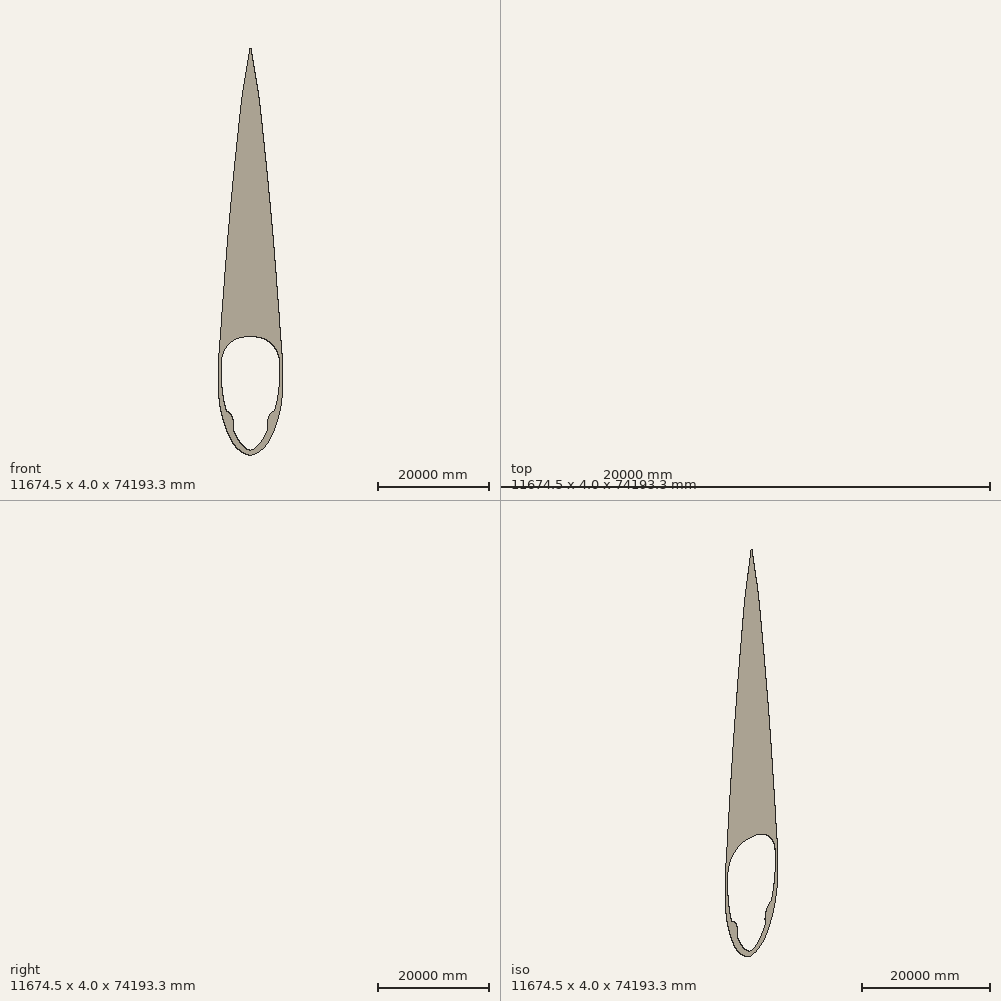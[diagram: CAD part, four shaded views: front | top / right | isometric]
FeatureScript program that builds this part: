
annotation { "Feature Type Name" : "Feature", "Feature Type Description" : "" }
export const myFeature = defineFeature(function(context is Context, id is Id, definition is map)
    precondition{}
    {
        {
            var Q0;
            Q0=qCreatedBy(makeId("Front.planeOp"),FACE);
            var sketch = newSketch(context, id + "F0", { "sketchPlane" : qUnion([Q0])});
            skLineSegment(sketch, "E0", {"start": v(0, -37096.65) * mm, "end": v(-23.06, -36971.76) * mm});
            skLineSegment(sketch, "E1", {"start": v(-23.06, -36971.76) * mm, "end": v(0, -37096.65) * mm});
            skLineSegment(sketch, "E2", {"start": v(0, -37096.65) * mm, "end": v(-199.5, -37059.82) * mm});
            skLineSegment(sketch, "E3", {"start": v(-199.5, -37059.82) * mm, "end": v(-412.04, -37002.75) * mm});
            skLineSegment(sketch, "E4", {"start": v(-412.04, -37002.75) * mm, "end": v(-621.33, -36933.84) * mm});
            skLineSegment(sketch, "E5", {"start": v(-621.33, -36933.84) * mm, "end": v(-815.34, -36864.47) * mm});
            skLineSegment(sketch, "E6", {"start": v(-815.34, -36864.47) * mm, "end": v(-1006.9, -36788.7) * mm});
            skLineSegment(sketch, "E7", {"start": v(-1006.9, -36788.7) * mm, "end": v(-1256.13, -36672.62) * mm});
            skLineSegment(sketch, "E8", {"start": v(-1256.13, -36672.62) * mm, "end": v(-1493.88, -36535.36) * mm});
            skLineSegment(sketch, "E9", {"start": v(-1493.88, -36535.36) * mm, "end": v(-1681.02, -36403.79) * mm});
            skLineSegment(sketch, "E10", {"start": v(-1681.02, -36403.79) * mm, "end": v(-1862.46, -36263.7) * mm});
            skLineSegment(sketch, "E11", {"start": v(-1862.46, -36263.7) * mm, "end": v(-2090.12, -36083.09) * mm});
            skLineSegment(sketch, "E12", {"start": v(-2090.12, -36083.09) * mm, "end": v(-2309.52, -35893.5) * mm});
            skLineSegment(sketch, "E13", {"start": v(-2309.52, -35893.5) * mm, "end": v(-2502.76, -35700.77) * mm});
            skLineSegment(sketch, "E14", {"start": v(-2502.76, -35700.77) * mm, "end": v(-2686.25, -35497.97) * mm});
            skLineSegment(sketch, "E15", {"start": v(-2686.25, -35497.97) * mm, "end": v(-2852.5, -35302.42) * mm});
            skLineSegment(sketch, "E16", {"start": v(-2852.5, -35302.42) * mm, "end": v(-3008.15, -35098.91) * mm});
            skLineSegment(sketch, "E17", {"start": v(-3008.15, -35098.91) * mm, "end": v(-3148.76, -34887.5) * mm});
            skLineSegment(sketch, "E18", {"start": v(-3148.76, -34887.5) * mm, "end": v(-3283.5, -34672.02) * mm});
            skLineSegment(sketch, "E19", {"start": v(-3283.5, -34672.02) * mm, "end": v(-3175.84, -34604.68) * mm});
            skLineSegment(sketch, "E20", {"start": v(-3175.84, -34604.68) * mm, "end": v(-3283.5, -34672.02) * mm});
            skLineSegment(sketch, "E21", {"start": v(-3283.5, -34672.02) * mm, "end": v(-3291.13, -34659.95) * mm});
            skLineSegment(sketch, "E22", {"start": v(-3291.13, -34659.95) * mm, "end": v(-3183.46, -34592.62) * mm});
            skLineSegment(sketch, "E23", {"start": v(-3183.46, -34592.62) * mm, "end": v(-3291.13, -34659.95) * mm});
            skLineSegment(sketch, "E24", {"start": v(-3291.13, -34659.95) * mm, "end": v(-3416.73, -34462.67) * mm});
            skLineSegment(sketch, "E25", {"start": v(-3416.73, -34462.67) * mm, "end": v(-3537.36, -34262.54) * mm});
            skLineSegment(sketch, "E26", {"start": v(-3537.36, -34262.54) * mm, "end": v(-3671.16, -34003.59) * mm});
            skLineSegment(sketch, "E27", {"start": v(-3671.16, -34003.59) * mm, "end": v(-3795.65, -33739.48) * mm});
            skLineSegment(sketch, "E28", {"start": v(-3795.65, -33739.48) * mm, "end": v(-3922.1, -33474.79) * mm});
            skLineSegment(sketch, "E29", {"start": v(-3922.1, -33474.79) * mm, "end": v(-4045.76, -33209.05) * mm});
            skLineSegment(sketch, "E30", {"start": v(-4045.76, -33209.05) * mm, "end": v(-4144.21, -32979.77) * mm});
            skLineSegment(sketch, "E31", {"start": v(-4144.21, -32979.77) * mm, "end": v(-4236.97, -32748.02) * mm});
            skLineSegment(sketch, "E32", {"start": v(-4236.97, -32748.02) * mm, "end": v(-4415.51, -32278.83) * mm});
            skLineSegment(sketch, "E33", {"start": v(-4415.51, -32278.83) * mm, "end": v(-4513.17, -32023.6) * mm});
            skLineSegment(sketch, "E34", {"start": v(-4513.17, -32023.6) * mm, "end": v(-4608.2, -31767.42) * mm});
            skLineSegment(sketch, "E35", {"start": v(-4608.2, -31767.42) * mm, "end": v(-4705.45, -31481.47) * mm});
            skLineSegment(sketch, "E36", {"start": v(-4705.45, -31481.47) * mm, "end": v(-4795.6, -31193.16) * mm});
            skLineSegment(sketch, "E37", {"start": v(-4795.6, -31193.16) * mm, "end": v(-4908.47, -30801.92) * mm});
            skLineSegment(sketch, "E38", {"start": v(-4908.47, -30801.92) * mm, "end": v(-4786.45, -30766.72) * mm});
            skLineSegment(sketch, "E39", {"start": v(-4786.45, -30766.72) * mm, "end": v(-4908.47, -30801.92) * mm});
            skLineSegment(sketch, "E40", {"start": v(-4908.47, -30801.92) * mm, "end": v(-4964.13, -30600.88) * mm});
            skLineSegment(sketch, "E41", {"start": v(-4964.13, -30600.88) * mm, "end": v(-5135.78, -29969.28) * mm});
            skLineSegment(sketch, "E42", {"start": v(-5135.78, -29969.28) * mm, "end": v(-5236.18, -29587.47) * mm});
            skLineSegment(sketch, "E43", {"start": v(-5236.18, -29587.47) * mm, "end": v(-5325.57, -29203.14) * mm});
            skLineSegment(sketch, "E44", {"start": v(-5325.57, -29203.14) * mm, "end": v(-5382.36, -28908.63) * mm});
            skLineSegment(sketch, "E45", {"start": v(-5382.36, -28908.63) * mm, "end": v(-5437.78, -28613.76) * mm});
            skLineSegment(sketch, "E46", {"start": v(-5437.78, -28613.76) * mm, "end": v(-5477.92, -28417.57) * mm});
            skLineSegment(sketch, "E47", {"start": v(-5477.92, -28417.57) * mm, "end": v(-5516.47, -28221.15) * mm});
            skLineSegment(sketch, "E48", {"start": v(-5516.47, -28221.15) * mm, "end": v(-5570.14, -27874.09) * mm});
            skLineSegment(sketch, "E49", {"start": v(-5570.14, -27874.09) * mm, "end": v(-5613.73, -27525.35) * mm});
            skLineSegment(sketch, "E50", {"start": v(-5613.73, -27525.35) * mm, "end": v(-5665.85, -27100.86) * mm});
            skLineSegment(sketch, "E51", {"start": v(-5665.85, -27100.86) * mm, "end": v(-5713.76, -26676.05) * mm});
            skLineSegment(sketch, "E52", {"start": v(-5713.76, -26676.05) * mm, "end": v(-5587.57, -26661.8) * mm});
            skLineSegment(sketch, "E53", {"start": v(-5587.57, -26661.8) * mm, "end": v(-5713.76, -26676.05) * mm});
            skLineSegment(sketch, "E54", {"start": v(-5713.76, -26676.05) * mm, "end": v(-5718, -26633.9) * mm});
            skLineSegment(sketch, "E55", {"start": v(-5718, -26633.9) * mm, "end": v(-5752.41, -26236.68) * mm});
            skLineSegment(sketch, "E56", {"start": v(-5752.41, -26236.68) * mm, "end": v(-5778.7, -25838.78) * mm});
            skLineSegment(sketch, "E57", {"start": v(-5778.7, -25838.78) * mm, "end": v(-5800.12, -25414.8) * mm});
            skLineSegment(sketch, "E58", {"start": v(-5800.12, -25414.8) * mm, "end": v(-5815.13, -24990.58) * mm});
            skLineSegment(sketch, "E59", {"start": v(-5815.13, -24990.58) * mm, "end": v(-5830.06, -24103.63) * mm});
            skLineSegment(sketch, "E60", {"start": v(-5830.06, -24103.63) * mm, "end": v(-5837.25, -22774.4) * mm});
            skLineSegment(sketch, "E61", {"start": v(-5837.25, -22774.4) * mm, "end": v(-5835.85, -22468.92) * mm});
            skLineSegment(sketch, "E62", {"start": v(-5835.85, -22468.92) * mm, "end": v(-5708.85, -22469.5) * mm});
            skLineSegment(sketch, "E63", {"start": v(-5708.85, -22469.5) * mm, "end": v(-5835.85, -22468.92) * mm});
            skLineSegment(sketch, "E64", {"start": v(-5835.85, -22468.92) * mm, "end": v(-5824.1, -21345.02) * mm});
            skLineSegment(sketch, "E65", {"start": v(-5824.1, -21345.02) * mm, "end": v(-5817.29, -20813.75) * mm});
            skLineSegment(sketch, "E66", {"start": v(-5817.29, -20813.75) * mm, "end": v(-5805.37, -20282.59) * mm});
            skLineSegment(sketch, "E67", {"start": v(-5805.37, -20282.59) * mm, "end": v(-5782.67, -19739.46) * mm});
            skLineSegment(sketch, "E68", {"start": v(-5782.67, -19739.46) * mm, "end": v(-5747.26, -19197.02) * mm});
            skLineSegment(sketch, "E69", {"start": v(-5747.26, -19197.02) * mm, "end": v(-5713.76, -18798.26) * mm});
            skLineSegment(sketch, "E70", {"start": v(-5713.76, -18798.26) * mm, "end": v(-5680.74, -18399.48) * mm});
            skLineSegment(sketch, "E71", {"start": v(-5680.74, -18399.48) * mm, "end": v(-5670.8, -18263.2) * mm});
            skLineSegment(sketch, "E72", {"start": v(-5670.8, -18263.2) * mm, "end": v(-5544.13, -18272.43) * mm});
            skLineSegment(sketch, "E73", {"start": v(-5544.13, -18272.43) * mm, "end": v(-5670.8, -18263.2) * mm});
            skLineSegment(sketch, "E74", {"start": v(-5670.8, -18263.2) * mm, "end": v(-5626.79, -17613.9) * mm});
            skLineSegment(sketch, "E75", {"start": v(-5626.79, -17613.9) * mm, "end": v(-5564.33, -16875.94) * mm});
            skLineSegment(sketch, "E76", {"start": v(-5564.33, -16875.94) * mm, "end": v(-5451.63, -15470.8) * mm});
            skLineSegment(sketch, "E77", {"start": v(-5451.63, -15470.8) * mm, "end": v(-5351.12, -14064.74) * mm});
            skLineSegment(sketch, "E78", {"start": v(-5351.12, -14064.74) * mm, "end": v(-5224.45, -14073.78) * mm});
            skLineSegment(sketch, "E79", {"start": v(-5224.45, -14073.78) * mm, "end": v(-5351.12, -14064.74) * mm});
            skLineSegment(sketch, "E80", {"start": v(-5351.12, -14064.74) * mm, "end": v(-5174.97, -11416.08) * mm});
            skLineSegment(sketch, "E81", {"start": v(-5174.97, -11416.08) * mm, "end": v(-5048.25, -11424.51) * mm});
            skLineSegment(sketch, "E82", {"start": v(-5048.25, -11424.51) * mm, "end": v(-5174.97, -11416.08) * mm});
            skLineSegment(sketch, "E83", {"start": v(-5174.97, -11416.08) * mm, "end": v(-4896.69, -7799.65) * mm});
            skLineSegment(sketch, "E84", {"start": v(-4896.69, -7799.65) * mm, "end": v(-4770.04, -7809.4) * mm});
            skLineSegment(sketch, "E85", {"start": v(-4770.04, -7809.4) * mm, "end": v(-4896.69, -7799.65) * mm});
            skLineSegment(sketch, "E86", {"start": v(-4896.69, -7799.65) * mm, "end": v(-4548.63, -3176.4) * mm});
            skLineSegment(sketch, "E87", {"start": v(-4548.63, -3176.4) * mm, "end": v(-4421.99, -3185.92) * mm});
            skLineSegment(sketch, "E88", {"start": v(-4421.99, -3185.92) * mm, "end": v(-4548.63, -3176.4) * mm});
            skLineSegment(sketch, "E89", {"start": v(-4548.63, -3176.4) * mm, "end": v(-4097.3, 2407.44) * mm});
            skLineSegment(sketch, "E90", {"start": v(-4097.3, 2407.44) * mm, "end": v(-3970.73, 2397.2) * mm});
            skLineSegment(sketch, "E91", {"start": v(-3970.73, 2397.2) * mm, "end": v(-4097.3, 2407.44) * mm});
            skLineSegment(sketch, "E92", {"start": v(-4097.3, 2407.44) * mm, "end": v(-3754.7, 6281.67) * mm});
            skLineSegment(sketch, "E93", {"start": v(-3754.7, 6281.67) * mm, "end": v(-3628.21, 6270.5) * mm});
            skLineSegment(sketch, "E94", {"start": v(-3628.21, 6270.5) * mm, "end": v(-3754.7, 6281.67) * mm});
            skLineSegment(sketch, "E95", {"start": v(-3754.7, 6281.67) * mm, "end": v(-3346.15, 10484.71) * mm});
            skLineSegment(sketch, "E96", {"start": v(-3346.15, 10484.71) * mm, "end": v(-3219.75, 10472.42) * mm});
            skLineSegment(sketch, "E97", {"start": v(-3219.75, 10472.42) * mm, "end": v(-3346.15, 10484.71) * mm});
            skLineSegment(sketch, "E98", {"start": v(-3346.15, 10484.71) * mm, "end": v(-3071.3, 13448.2) * mm});
            skLineSegment(sketch, "E99", {"start": v(-3071.3, 13448.2) * mm, "end": v(-2944.83, 13436.47) * mm});
            skLineSegment(sketch, "E100", {"start": v(-2944.83, 13436.47) * mm, "end": v(-3071.3, 13448.2) * mm});
            skLineSegment(sketch, "E101", {"start": v(-3071.3, 13448.2) * mm, "end": v(-3028.06, 13918.2) * mm});
            skLineSegment(sketch, "E102", {"start": v(-3028.06, 13918.2) * mm, "end": v(-2984.83, 14278.46) * mm});
            skLineSegment(sketch, "E103", {"start": v(-2984.83, 14278.46) * mm, "end": v(-2942.77, 14638.8) * mm});
            skLineSegment(sketch, "E104", {"start": v(-2942.77, 14638.8) * mm, "end": v(-2910.05, 15016.99) * mm});
            skLineSegment(sketch, "E105", {"start": v(-2910.05, 15016.99) * mm, "end": v(-2879.8, 15395.47) * mm});
            skLineSegment(sketch, "E106", {"start": v(-2879.8, 15395.47) * mm, "end": v(-2810.46, 16049.37) * mm});
            skLineSegment(sketch, "E107", {"start": v(-2810.46, 16049.37) * mm, "end": v(-2718.18, 16865.3) * mm});
            skLineSegment(sketch, "E108", {"start": v(-2718.18, 16865.3) * mm, "end": v(-2641.02, 17547.39) * mm});
            skLineSegment(sketch, "E109", {"start": v(-2641.02, 17547.39) * mm, "end": v(-2602.15, 17952.92) * mm});
            skLineSegment(sketch, "E110", {"start": v(-2602.15, 17952.92) * mm, "end": v(-2564.33, 18358.56) * mm});
            skLineSegment(sketch, "E111", {"start": v(-2564.33, 18358.56) * mm, "end": v(-2476.75, 19167.53) * mm});
            skLineSegment(sketch, "E112", {"start": v(-2476.75, 19167.53) * mm, "end": v(-2368.14, 20139.23) * mm});
            skLineSegment(sketch, "E113", {"start": v(-2368.14, 20139.23) * mm, "end": v(-2264.77, 21133.64) * mm});
            skLineSegment(sketch, "E114", {"start": v(-2264.77, 21133.64) * mm, "end": v(-2207.67, 21721.47) * mm});
            skLineSegment(sketch, "E115", {"start": v(-2207.67, 21721.47) * mm, "end": v(-2148.26, 22309.05) * mm});
            skLineSegment(sketch, "E116", {"start": v(-2148.26, 22309.05) * mm, "end": v(-2083.49, 22880.75) * mm});
            skLineSegment(sketch, "E117", {"start": v(-2083.49, 22880.75) * mm, "end": v(-2012.62, 23451.72) * mm});
            skLineSegment(sketch, "E118", {"start": v(-2012.62, 23451.72) * mm, "end": v(-1886.59, 23436.07) * mm});
            skLineSegment(sketch, "E119", {"start": v(-1886.59, 23436.07) * mm, "end": v(-2012.62, 23451.72) * mm});
            skLineSegment(sketch, "E120", {"start": v(-2012.62, 23451.72) * mm, "end": v(-1891.87, 24679.91) * mm});
            skLineSegment(sketch, "E121", {"start": v(-1891.87, 24679.91) * mm, "end": v(-1792.53, 25579.78) * mm});
            skLineSegment(sketch, "E122", {"start": v(-1792.53, 25579.78) * mm, "end": v(-1687.32, 26479.02) * mm});
            skLineSegment(sketch, "E123", {"start": v(-1687.32, 26479.02) * mm, "end": v(-1555.85, 27559.4) * mm});
            skLineSegment(sketch, "E124", {"start": v(-1555.85, 27559.4) * mm, "end": v(-1408.96, 28637.64) * mm});
            skLineSegment(sketch, "E125", {"start": v(-1408.96, 28637.64) * mm, "end": v(-1272.31, 29508.48) * mm});
            skLineSegment(sketch, "E126", {"start": v(-1272.31, 29508.48) * mm, "end": v(-1126.57, 30377.94) * mm});
            skLineSegment(sketch, "E127", {"start": v(-1126.57, 30377.94) * mm, "end": v(-728.8, 32712.89) * mm});
            skLineSegment(sketch, "E128", {"start": v(-728.8, 32712.89) * mm, "end": v(-528.1, 33866.25) * mm});
            skLineSegment(sketch, "E129", {"start": v(-528.1, 33866.25) * mm, "end": v(-338.79, 35021.55) * mm});
            skLineSegment(sketch, "E130", {"start": v(-338.79, 35021.55) * mm, "end": v(-210.34, 35879.74) * mm});
            skLineSegment(sketch, "E131", {"start": v(-210.34, 35879.74) * mm, "end": v(-69.32, 36735.74) * mm});
            skLineSegment(sketch, "E132", {"start": v(-69.32, 36735.74) * mm, "end": v(0, 37096.65) * mm});
            skLineSegment(sketch, "E133", {"start": v(0, 37096.65) * mm, "end": v(69.34, 36735.74) * mm});
            skLineSegment(sketch, "E134", {"start": v(69.34, 36735.74) * mm, "end": v(210.34, 35879.74) * mm});
            skLineSegment(sketch, "E135", {"start": v(210.34, 35879.74) * mm, "end": v(338.79, 35021.55) * mm});
            skLineSegment(sketch, "E136", {"start": v(338.79, 35021.55) * mm, "end": v(528.12, 33866.25) * mm});
            skLineSegment(sketch, "E137", {"start": v(528.12, 33866.25) * mm, "end": v(728.8, 32712.89) * mm});
            skLineSegment(sketch, "E138", {"start": v(728.8, 32712.89) * mm, "end": v(1126.57, 30377.94) * mm});
            skLineSegment(sketch, "E139", {"start": v(1126.57, 30377.94) * mm, "end": v(1272.31, 29508.48) * mm});
            skLineSegment(sketch, "E140", {"start": v(1272.31, 29508.48) * mm, "end": v(1408.96, 28637.64) * mm});
            skLineSegment(sketch, "E141", {"start": v(1408.96, 28637.64) * mm, "end": v(1555.85, 27559.4) * mm});
            skLineSegment(sketch, "E142", {"start": v(1555.85, 27559.4) * mm, "end": v(1687.32, 26479.02) * mm});
            skLineSegment(sketch, "E143", {"start": v(1687.32, 26479.02) * mm, "end": v(1792.53, 25579.78) * mm});
            skLineSegment(sketch, "E144", {"start": v(1792.53, 25579.78) * mm, "end": v(1891.87, 24679.91) * mm});
            skLineSegment(sketch, "E145", {"start": v(1891.87, 24679.91) * mm, "end": v(2012.62, 23451.72) * mm});
            skLineSegment(sketch, "E146", {"start": v(2012.62, 23451.72) * mm, "end": v(1886.23, 23439.27) * mm});
            skLineSegment(sketch, "E147", {"start": v(1886.23, 23439.27) * mm, "end": v(2012.62, 23451.72) * mm});
            skLineSegment(sketch, "E148", {"start": v(2012.62, 23451.72) * mm, "end": v(2083.51, 22880.75) * mm});
            skLineSegment(sketch, "E149", {"start": v(2083.51, 22880.75) * mm, "end": v(2148.26, 22309.05) * mm});
            skLineSegment(sketch, "E150", {"start": v(2148.26, 22309.05) * mm, "end": v(2207.67, 21721.47) * mm});
            skLineSegment(sketch, "E151", {"start": v(2207.67, 21721.47) * mm, "end": v(2264.77, 21133.64) * mm});
            skLineSegment(sketch, "E152", {"start": v(2264.77, 21133.64) * mm, "end": v(2368.14, 20139.23) * mm});
            skLineSegment(sketch, "E153", {"start": v(2368.14, 20139.23) * mm, "end": v(2476.75, 19167.53) * mm});
            skLineSegment(sketch, "E154", {"start": v(2476.75, 19167.53) * mm, "end": v(2564.33, 18358.56) * mm});
            skLineSegment(sketch, "E155", {"start": v(2564.33, 18358.56) * mm, "end": v(2602.15, 17952.92) * mm});
            skLineSegment(sketch, "E156", {"start": v(2602.15, 17952.92) * mm, "end": v(2641.02, 17547.39) * mm});
            skLineSegment(sketch, "E157", {"start": v(2641.02, 17547.39) * mm, "end": v(2718.18, 16865.3) * mm});
            skLineSegment(sketch, "E158", {"start": v(2718.18, 16865.3) * mm, "end": v(2810.46, 16049.37) * mm});
            skLineSegment(sketch, "E159", {"start": v(2810.46, 16049.37) * mm, "end": v(2879.8, 15395.47) * mm});
            skLineSegment(sketch, "E160", {"start": v(2879.8, 15395.47) * mm, "end": v(2910.08, 15016.99) * mm});
            skLineSegment(sketch, "E161", {"start": v(2910.08, 15016.99) * mm, "end": v(2942.77, 14638.8) * mm});
            skLineSegment(sketch, "E162", {"start": v(2942.77, 14638.8) * mm, "end": v(2984.83, 14278.46) * mm});
            skLineSegment(sketch, "E163", {"start": v(2984.83, 14278.46) * mm, "end": v(3028.06, 13918.2) * mm});
            skLineSegment(sketch, "E164", {"start": v(3028.06, 13918.2) * mm, "end": v(3071.3, 13448.2) * mm});
            skLineSegment(sketch, "E165", {"start": v(3071.3, 13448.2) * mm, "end": v(2944.83, 13436.55) * mm});
            skLineSegment(sketch, "E166", {"start": v(2944.83, 13436.55) * mm, "end": v(3071.3, 13448.2) * mm});
            skLineSegment(sketch, "E167", {"start": v(3071.3, 13448.2) * mm, "end": v(3346.17, 10484.71) * mm});
            skLineSegment(sketch, "E168", {"start": v(3346.17, 10484.71) * mm, "end": v(3219.7, 10472.98) * mm});
            skLineSegment(sketch, "E169", {"start": v(3219.7, 10472.98) * mm, "end": v(3346.17, 10484.71) * mm});
            skLineSegment(sketch, "E170", {"start": v(3346.17, 10484.71) * mm, "end": v(3754.7, 6281.67) * mm});
            skLineSegment(sketch, "E171", {"start": v(3754.7, 6281.67) * mm, "end": v(3628.31, 6269.4) * mm});
            skLineSegment(sketch, "E172", {"start": v(3628.31, 6269.4) * mm, "end": v(3754.7, 6281.67) * mm});
            skLineSegment(sketch, "E173", {"start": v(3754.7, 6281.67) * mm, "end": v(4097.32, 2407.44) * mm});
            skLineSegment(sketch, "E174", {"start": v(4097.32, 2407.44) * mm, "end": v(3970.8, 2396.26) * mm});
            skLineSegment(sketch, "E175", {"start": v(3970.8, 2396.26) * mm, "end": v(4097.32, 2407.44) * mm});
            skLineSegment(sketch, "E176", {"start": v(4097.32, 2407.44) * mm, "end": v(4548.63, -3176.4) * mm});
            skLineSegment(sketch, "E177", {"start": v(4548.63, -3176.4) * mm, "end": v(4422.06, -3186.63) * mm});
            skLineSegment(sketch, "E178", {"start": v(4422.06, -3186.63) * mm, "end": v(4548.63, -3176.4) * mm});
            skLineSegment(sketch, "E179", {"start": v(4548.63, -3176.4) * mm, "end": v(4896.69, -7799.65) * mm});
            skLineSegment(sketch, "E180", {"start": v(4896.69, -7799.65) * mm, "end": v(4770.04, -7809.2) * mm});
            skLineSegment(sketch, "E181", {"start": v(4770.04, -7809.2) * mm, "end": v(4896.69, -7799.65) * mm});
            skLineSegment(sketch, "E182", {"start": v(4896.69, -7799.65) * mm, "end": v(5175, -11416.08) * mm});
            skLineSegment(sketch, "E183", {"start": v(5175, -11416.08) * mm, "end": v(5048.35, -11425.83) * mm});
            skLineSegment(sketch, "E184", {"start": v(5048.35, -11425.83) * mm, "end": v(5175, -11416.08) * mm});
            skLineSegment(sketch, "E185", {"start": v(5175, -11416.08) * mm, "end": v(5351.12, -14064.74) * mm});
            skLineSegment(sketch, "E186", {"start": v(5351.12, -14064.74) * mm, "end": v(5224.4, -14073.15) * mm});
            skLineSegment(sketch, "E187", {"start": v(5224.4, -14073.15) * mm, "end": v(5351.12, -14064.74) * mm});
            skLineSegment(sketch, "E188", {"start": v(5351.12, -14064.74) * mm, "end": v(5451.63, -15470.8) * mm});
            skLineSegment(sketch, "E189", {"start": v(5451.63, -15470.8) * mm, "end": v(5564.33, -16875.94) * mm});
            skLineSegment(sketch, "E190", {"start": v(5564.33, -16875.94) * mm, "end": v(5626.79, -17613.9) * mm});
            skLineSegment(sketch, "E191", {"start": v(5626.79, -17613.9) * mm, "end": v(5670.8, -18263.2) * mm});
            skLineSegment(sketch, "E192", {"start": v(5670.8, -18263.2) * mm, "end": v(5544.1, -18271.8) * mm});
            skLineSegment(sketch, "E193", {"start": v(5544.1, -18271.8) * mm, "end": v(5670.8, -18263.2) * mm});
            skLineSegment(sketch, "E194", {"start": v(5670.8, -18263.2) * mm, "end": v(5680.74, -18399.48) * mm});
            skLineSegment(sketch, "E195", {"start": v(5680.74, -18399.48) * mm, "end": v(5713.76, -18798.26) * mm});
            skLineSegment(sketch, "E196", {"start": v(5713.76, -18798.26) * mm, "end": v(5747.26, -19197.02) * mm});
            skLineSegment(sketch, "E197", {"start": v(5747.26, -19197.02) * mm, "end": v(5782.67, -19739.46) * mm});
            skLineSegment(sketch, "E198", {"start": v(5782.67, -19739.46) * mm, "end": v(5805.37, -20282.59) * mm});
            skLineSegment(sketch, "E199", {"start": v(5805.37, -20282.59) * mm, "end": v(5817.29, -20813.75) * mm});
            skLineSegment(sketch, "E200", {"start": v(5817.29, -20813.75) * mm, "end": v(5824.1, -21345.02) * mm});
            skLineSegment(sketch, "E201", {"start": v(5824.1, -21345.02) * mm, "end": v(5835.85, -22468.9) * mm});
            skLineSegment(sketch, "E202", {"start": v(5835.85, -22468.9) * mm, "end": v(5708.85, -22470.24) * mm});
            skLineSegment(sketch, "E203", {"start": v(5708.85, -22470.24) * mm, "end": v(5835.85, -22468.9) * mm});
            skLineSegment(sketch, "E204", {"start": v(5835.85, -22468.9) * mm, "end": v(5837.25, -22774.4) * mm});
            skLineSegment(sketch, "E205", {"start": v(5837.25, -22774.4) * mm, "end": v(5830.06, -24103.63) * mm});
            skLineSegment(sketch, "E206", {"start": v(5830.06, -24103.63) * mm, "end": v(5815.13, -24990.58) * mm});
            skLineSegment(sketch, "E207", {"start": v(5815.13, -24990.58) * mm, "end": v(5800.12, -25414.8) * mm});
            skLineSegment(sketch, "E208", {"start": v(5800.12, -25414.8) * mm, "end": v(5778.7, -25838.78) * mm});
            skLineSegment(sketch, "E209", {"start": v(5778.7, -25838.78) * mm, "end": v(5752.41, -26236.68) * mm});
            skLineSegment(sketch, "E210", {"start": v(5752.41, -26236.68) * mm, "end": v(5718, -26633.9) * mm});
            skLineSegment(sketch, "E211", {"start": v(5718, -26633.9) * mm, "end": v(5713.76, -26676.02) * mm});
            skLineSegment(sketch, "E212", {"start": v(5713.76, -26676.02) * mm, "end": v(5587.4, -26663.32) * mm});
            skLineSegment(sketch, "E213", {"start": v(5587.4, -26663.32) * mm, "end": v(5713.76, -26676.02) * mm});
            skLineSegment(sketch, "E214", {"start": v(5713.76, -26676.02) * mm, "end": v(5665.85, -27100.86) * mm});
            skLineSegment(sketch, "E215", {"start": v(5665.85, -27100.86) * mm, "end": v(5613.73, -27525.35) * mm});
            skLineSegment(sketch, "E216", {"start": v(5613.73, -27525.35) * mm, "end": v(5570.14, -27874.09) * mm});
            skLineSegment(sketch, "E217", {"start": v(5570.14, -27874.09) * mm, "end": v(5516.47, -28221.15) * mm});
            skLineSegment(sketch, "E218", {"start": v(5516.47, -28221.15) * mm, "end": v(5477.92, -28417.57) * mm});
            skLineSegment(sketch, "E219", {"start": v(5477.92, -28417.57) * mm, "end": v(5437.78, -28613.76) * mm});
            skLineSegment(sketch, "E220", {"start": v(5437.78, -28613.76) * mm, "end": v(5382.36, -28908.63) * mm});
            skLineSegment(sketch, "E221", {"start": v(5382.36, -28908.63) * mm, "end": v(5325.57, -29203.14) * mm});
            skLineSegment(sketch, "E222", {"start": v(5325.57, -29203.14) * mm, "end": v(5236.18, -29587.47) * mm});
            skLineSegment(sketch, "E223", {"start": v(5236.18, -29587.47) * mm, "end": v(5135.78, -29969.28) * mm});
            skLineSegment(sketch, "E224", {"start": v(5135.78, -29969.28) * mm, "end": v(4964.15, -30600.88) * mm});
            skLineSegment(sketch, "E225", {"start": v(4964.15, -30600.88) * mm, "end": v(4908.47, -30801.92) * mm});
            skLineSegment(sketch, "E226", {"start": v(4908.47, -30801.92) * mm, "end": v(4786.07, -30768.01) * mm});
            skLineSegment(sketch, "E227", {"start": v(4786.07, -30768.01) * mm, "end": v(4908.47, -30801.92) * mm});
            skLineSegment(sketch, "E228", {"start": v(4908.47, -30801.92) * mm, "end": v(4795.6, -31193.16) * mm});
            skLineSegment(sketch, "E229", {"start": v(4795.6, -31193.16) * mm, "end": v(4705.45, -31481.47) * mm});
            skLineSegment(sketch, "E230", {"start": v(4705.45, -31481.47) * mm, "end": v(4608.2, -31767.42) * mm});
            skLineSegment(sketch, "E231", {"start": v(4608.2, -31767.42) * mm, "end": v(4513.17, -32023.6) * mm});
            skLineSegment(sketch, "E232", {"start": v(4513.17, -32023.6) * mm, "end": v(4415.51, -32278.83) * mm});
            skLineSegment(sketch, "E233", {"start": v(4415.51, -32278.83) * mm, "end": v(4236.97, -32748.02) * mm});
            skLineSegment(sketch, "E234", {"start": v(4236.97, -32748.02) * mm, "end": v(4144.21, -32979.77) * mm});
            skLineSegment(sketch, "E235", {"start": v(4144.21, -32979.77) * mm, "end": v(4045.79, -33209.05) * mm});
            skLineSegment(sketch, "E236", {"start": v(4045.79, -33209.05) * mm, "end": v(3922.1, -33474.79) * mm});
            skLineSegment(sketch, "E237", {"start": v(3922.1, -33474.79) * mm, "end": v(3795.65, -33739.48) * mm});
            skLineSegment(sketch, "E238", {"start": v(3795.65, -33739.48) * mm, "end": v(3671.16, -34003.59) * mm});
            skLineSegment(sketch, "E239", {"start": v(3671.16, -34003.59) * mm, "end": v(3537.36, -34262.54) * mm});
            skLineSegment(sketch, "E240", {"start": v(3537.36, -34262.54) * mm, "end": v(3416.73, -34462.67) * mm});
            skLineSegment(sketch, "E241", {"start": v(3416.73, -34462.67) * mm, "end": v(3291.13, -34659.95) * mm});
            skLineSegment(sketch, "E242", {"start": v(3291.13, -34659.95) * mm, "end": v(3283.53, -34672.02) * mm});
            skLineSegment(sketch, "E243", {"start": v(3283.53, -34672.02) * mm, "end": v(3176.1, -34604.3) * mm});
            skLineSegment(sketch, "E244", {"start": v(3176.1, -34604.3) * mm, "end": v(3283.53, -34672.02) * mm});
            skLineSegment(sketch, "E245", {"start": v(3283.53, -34672.02) * mm, "end": v(3148.79, -34887.5) * mm});
            skLineSegment(sketch, "E246", {"start": v(3148.79, -34887.5) * mm, "end": v(3008.15, -35098.91) * mm});
            skLineSegment(sketch, "E247", {"start": v(3008.15, -35098.91) * mm, "end": v(2852.5, -35302.42) * mm});
            skLineSegment(sketch, "E248", {"start": v(2852.5, -35302.42) * mm, "end": v(2686.25, -35497.97) * mm});
            skLineSegment(sketch, "E249", {"start": v(2686.25, -35497.97) * mm, "end": v(2502.76, -35700.77) * mm});
            skLineSegment(sketch, "E250", {"start": v(2502.76, -35700.77) * mm, "end": v(2309.52, -35893.5) * mm});
            skLineSegment(sketch, "E251", {"start": v(2309.52, -35893.5) * mm, "end": v(2090.12, -36083.09) * mm});
            skLineSegment(sketch, "E252", {"start": v(2090.12, -36083.09) * mm, "end": v(1862.46, -36263.7) * mm});
            skLineSegment(sketch, "E253", {"start": v(1862.46, -36263.7) * mm, "end": v(1681.02, -36403.79) * mm});
            skLineSegment(sketch, "E254", {"start": v(1681.02, -36403.79) * mm, "end": v(1493.88, -36535.36) * mm});
            skLineSegment(sketch, "E255", {"start": v(1493.88, -36535.36) * mm, "end": v(1256.13, -36672.62) * mm});
            skLineSegment(sketch, "E256", {"start": v(1256.13, -36672.62) * mm, "end": v(1006.9, -36788.7) * mm});
            skLineSegment(sketch, "E257", {"start": v(1006.9, -36788.7) * mm, "end": v(815.34, -36864.47) * mm});
            skLineSegment(sketch, "E258", {"start": v(815.34, -36864.47) * mm, "end": v(621.33, -36933.84) * mm});
            skLineSegment(sketch, "E259", {"start": v(621.33, -36933.84) * mm, "end": v(412.04, -37002.75) * mm});
            skLineSegment(sketch, "E260", {"start": v(412.04, -37002.75) * mm, "end": v(199.5, -37059.82) * mm});
            skLineSegment(sketch, "E261", {"start": v(199.5, -37059.82) * mm, "end": v(0, -37096.65) * mm});
            skLineSegment(sketch, "E262", {"start": v(0, -36146.69) * mm, "end": v(-18.06, -36020.98) * mm});
            skLineSegment(sketch, "E263", {"start": v(-18.06, -36020.98) * mm, "end": v(0, -36146.69) * mm});
            skLineSegment(sketch, "E264", {"start": v(0, -36146.69) * mm, "end": v(-160.99, -36123.88) * mm});
            skLineSegment(sketch, "E265", {"start": v(-160.99, -36123.88) * mm, "end": v(-319.38, -36085.9) * mm});
            skLineSegment(sketch, "E266", {"start": v(-319.38, -36085.9) * mm, "end": v(-471.3, -36034.07) * mm});
            skLineSegment(sketch, "E267", {"start": v(-471.3, -36034.07) * mm, "end": v(-616.38, -35966.58) * mm});
            skLineSegment(sketch, "E268", {"start": v(-616.38, -35966.58) * mm, "end": v(-789.05, -35857.94) * mm});
            skLineSegment(sketch, "E269", {"start": v(-789.05, -35857.94) * mm, "end": v(-953.16, -35735.26) * mm});
            skLineSegment(sketch, "E270", {"start": v(-953.16, -35735.26) * mm, "end": v(-1062.3, -35649.92) * mm});
            skLineSegment(sketch, "E271", {"start": v(-1062.3, -35649.92) * mm, "end": v(-1167.54, -35560.33) * mm});
            skLineSegment(sketch, "E272", {"start": v(-1167.54, -35560.33) * mm, "end": v(-1313.36, -35415.17) * mm});
            skLineSegment(sketch, "E273", {"start": v(-1313.36, -35415.17) * mm, "end": v(-1519.15, -35190.89) * mm});
            skLineSegment(sketch, "E274", {"start": v(-1519.15, -35190.89) * mm, "end": v(-1685.24, -34989.97) * mm});
            skLineSegment(sketch, "E275", {"start": v(-1685.24, -34989.97) * mm, "end": v(-1863.6, -34755.18) * mm});
            skLineSegment(sketch, "E276", {"start": v(-1863.6, -34755.18) * mm, "end": v(-1989.86, -34573.95) * mm});
            skLineSegment(sketch, "E277", {"start": v(-1989.86, -34573.95) * mm, "end": v(-2135.33, -34350.45) * mm});
            skLineSegment(sketch, "E278", {"start": v(-2135.33, -34350.45) * mm, "end": v(-2251.74, -34175.37) * mm});
            skLineSegment(sketch, "E279", {"start": v(-2251.74, -34175.37) * mm, "end": v(-2325.22, -34052.36) * mm});
            skLineSegment(sketch, "E280", {"start": v(-2325.22, -34052.36) * mm, "end": v(-2396.62, -33928) * mm});
            skLineSegment(sketch, "E281", {"start": v(-2396.62, -33928) * mm, "end": v(-2494.89, -33759.06) * mm});
            skLineSegment(sketch, "E282", {"start": v(-2494.89, -33759.06) * mm, "end": v(-2562.4, -33629.14) * mm});
            skLineSegment(sketch, "E283", {"start": v(-2562.4, -33629.14) * mm, "end": v(-2630.22, -33499.32) * mm});
            skLineSegment(sketch, "E284", {"start": v(-2630.22, -33499.32) * mm, "end": v(-2676.2, -33419.11) * mm});
            skLineSegment(sketch, "E285", {"start": v(-2676.2, -33419.11) * mm, "end": v(-2721.03, -33338.34) * mm});
            skLineSegment(sketch, "E286", {"start": v(-2721.03, -33338.34) * mm, "end": v(-2776.14, -33221.83) * mm});
            skLineSegment(sketch, "E287", {"start": v(-2776.14, -33221.83) * mm, "end": v(-2829.5, -33104.3) * mm});
            skLineSegment(sketch, "E288", {"start": v(-2829.5, -33104.3) * mm, "end": v(-2869.97, -33023.2) * mm});
            skLineSegment(sketch, "E289", {"start": v(-2869.97, -33023.2) * mm, "end": v(-2909.37, -32941.7) * mm});
            skLineSegment(sketch, "E290", {"start": v(-2909.37, -32941.7) * mm, "end": v(-2947.34, -32850.4) * mm});
            skLineSegment(sketch, "E291", {"start": v(-2947.34, -32850.4) * mm, "end": v(-2985.47, -32759.17) * mm});
            skLineSegment(sketch, "E292", {"start": v(-2985.47, -32759.17) * mm, "end": v(-3047.19, -32637.76) * mm});
            skLineSegment(sketch, "E293", {"start": v(-3047.19, -32637.76) * mm, "end": v(-2933.98, -32580.2) * mm});
            skLineSegment(sketch, "E294", {"start": v(-2933.98, -32580.2) * mm, "end": v(-3047.19, -32637.76) * mm});
            skLineSegment(sketch, "E295", {"start": v(-3047.19, -32637.76) * mm, "end": v(-3056.53, -32524.01) * mm});
            skLineSegment(sketch, "E296", {"start": v(-3056.53, -32524.01) * mm, "end": v(-3064.71, -32337.07) * mm});
            skLineSegment(sketch, "E297", {"start": v(-3064.71, -32337.07) * mm, "end": v(-3067.56, -32065.85) * mm});
            skLineSegment(sketch, "E298", {"start": v(-3067.56, -32065.85) * mm, "end": v(-2940.56, -32064.5) * mm});
            skLineSegment(sketch, "E299", {"start": v(-2940.56, -32064.5) * mm, "end": v(-3067.56, -32065.85) * mm});
            skLineSegment(sketch, "E300", {"start": v(-3067.56, -32065.85) * mm, "end": v(-3041.93, -31972.3) * mm});
            skLineSegment(sketch, "E301", {"start": v(-3041.93, -31972.3) * mm, "end": v(-3022.22, -31877.3) * mm});
            skLineSegment(sketch, "E302", {"start": v(-3022.22, -31877.3) * mm, "end": v(-3006.3, -31757.65) * mm});
            skLineSegment(sketch, "E303", {"start": v(-3006.3, -31757.65) * mm, "end": v(-2999.08, -31637.15) * mm});
            skLineSegment(sketch, "E304", {"start": v(-2999.08, -31637.15) * mm, "end": v(-3000.1, -31497.04) * mm});
            skLineSegment(sketch, "E305", {"start": v(-3000.1, -31497.04) * mm, "end": v(-3009.04, -31357.14) * mm});
            skLineSegment(sketch, "E306", {"start": v(-3009.04, -31357.14) * mm, "end": v(-3032.46, -31159.4) * mm});
            skLineSegment(sketch, "E307", {"start": v(-3032.46, -31159.4) * mm, "end": v(-3070.25, -30964.15) * mm});
            skLineSegment(sketch, "E308", {"start": v(-3070.25, -30964.15) * mm, "end": v(-3131.85, -30740.07) * mm});
            skLineSegment(sketch, "E309", {"start": v(-3131.85, -30740.07) * mm, "end": v(-3217.16, -30456.07) * mm});
            skLineSegment(sketch, "E310", {"start": v(-3217.16, -30456.07) * mm, "end": v(-3302.66, -30209.49) * mm});
            skLineSegment(sketch, "E311", {"start": v(-3302.66, -30209.49) * mm, "end": v(-3364.1, -30059.5) * mm});
            skLineSegment(sketch, "E312", {"start": v(-3364.1, -30059.5) * mm, "end": v(-3436.09, -29914.65) * mm});
            skLineSegment(sketch, "E313", {"start": v(-3436.09, -29914.65) * mm, "end": v(-3527.12, -29763.11) * mm});
            skLineSegment(sketch, "E314", {"start": v(-3527.12, -29763.11) * mm, "end": v(-3595.52, -29651.45) * mm});
            skLineSegment(sketch, "E315", {"start": v(-3595.52, -29651.45) * mm, "end": v(-3667.96, -29542.71) * mm});
            skLineSegment(sketch, "E316", {"start": v(-3667.96, -29542.71) * mm, "end": v(-3731.18, -29461.82) * mm});
            skLineSegment(sketch, "E317", {"start": v(-3731.18, -29461.82) * mm, "end": v(-3799.69, -29384.98) * mm});
            skLineSegment(sketch, "E318", {"start": v(-3799.69, -29384.98) * mm, "end": v(-3851.5, -29332.91) * mm});
            skLineSegment(sketch, "E319", {"start": v(-3851.5, -29332.91) * mm, "end": v(-3907.08, -29285.26) * mm});
            skLineSegment(sketch, "E320", {"start": v(-3907.08, -29285.26) * mm, "end": v(-4027.96, -29205.89) * mm});
            skLineSegment(sketch, "E321", {"start": v(-4027.96, -29205.89) * mm, "end": v(-4122.95, -29149.85) * mm});
            skLineSegment(sketch, "E322", {"start": v(-4122.95, -29149.85) * mm, "end": v(-4210, -29108.3) * mm});
            skLineSegment(sketch, "E323", {"start": v(-4210, -29108.3) * mm, "end": v(-4299.76, -29061.56) * mm});
            skLineSegment(sketch, "E324", {"start": v(-4299.76, -29061.56) * mm, "end": v(-4377.54, -29019.22) * mm});
            skLineSegment(sketch, "E325", {"start": v(-4377.54, -29019.22) * mm, "end": v(-4316.8, -28907.69) * mm});
            skLineSegment(sketch, "E326", {"start": v(-4316.8, -28907.69) * mm, "end": v(-4377.54, -29019.22) * mm});
            skLineSegment(sketch, "E327", {"start": v(-4377.54, -29019.22) * mm, "end": v(-4457.45, -28719.5) * mm});
            skLineSegment(sketch, "E328", {"start": v(-4457.45, -28719.5) * mm, "end": v(-4565.98, -28314.27) * mm});
            skLineSegment(sketch, "E329", {"start": v(-4565.98, -28314.27) * mm, "end": v(-4666.84, -27907.23) * mm});
            skLineSegment(sketch, "E330", {"start": v(-4666.84, -27907.23) * mm, "end": v(-4781.42, -27334.24) * mm});
            skLineSegment(sketch, "E331", {"start": v(-4781.42, -27334.24) * mm, "end": v(-4881.73, -26758.19) * mm});
            skLineSegment(sketch, "E332", {"start": v(-4881.73, -26758.19) * mm, "end": v(-4963.97, -26295.73) * mm});
            skLineSegment(sketch, "E333", {"start": v(-4963.97, -26295.73) * mm, "end": v(-4838.93, -26273.5) * mm});
            skLineSegment(sketch, "E334", {"start": v(-4838.93, -26273.5) * mm, "end": v(-4963.97, -26295.73) * mm});
            skLineSegment(sketch, "E335", {"start": v(-4963.97, -26295.73) * mm, "end": v(-5021.17, -25932.84) * mm});
            skLineSegment(sketch, "E336", {"start": v(-5021.17, -25932.84) * mm, "end": v(-5061.48, -25607.31) * mm});
            skLineSegment(sketch, "E337", {"start": v(-5061.48, -25607.31) * mm, "end": v(-5097.98, -25281.26) * mm});
            skLineSegment(sketch, "E338", {"start": v(-5097.98, -25281.26) * mm, "end": v(-5140.6, -24925) * mm});
            skLineSegment(sketch, "E339", {"start": v(-5140.6, -24925) * mm, "end": v(-5179.85, -24568.45) * mm});
            skLineSegment(sketch, "E340", {"start": v(-5179.85, -24568.45) * mm, "end": v(-5209.26, -24211.84) * mm});
            skLineSegment(sketch, "E341", {"start": v(-5209.26, -24211.84) * mm, "end": v(-5235.27, -23854.9) * mm});
            skLineSegment(sketch, "E342", {"start": v(-5235.27, -23854.9) * mm, "end": v(-5262.14, -23525.12) * mm});
            skLineSegment(sketch, "E343", {"start": v(-5262.14, -23525.12) * mm, "end": v(-5135.58, -23514.81) * mm});
            skLineSegment(sketch, "E344", {"start": v(-5135.58, -23514.81) * mm, "end": v(-5262.14, -23525.12) * mm});
            skLineSegment(sketch, "E345", {"start": v(-5262.14, -23525.12) * mm, "end": v(-5282.74, -23275.77) * mm});
            skLineSegment(sketch, "E346", {"start": v(-5282.74, -23275.77) * mm, "end": v(-5297.98, -23025.99) * mm});
            skLineSegment(sketch, "E347", {"start": v(-5297.98, -23025.99) * mm, "end": v(-5310.63, -22650.96) * mm});
            skLineSegment(sketch, "E348", {"start": v(-5310.63, -22650.96) * mm, "end": v(-5311.9, -22275.7) * mm});
            skLineSegment(sketch, "E349", {"start": v(-5311.9, -22275.7) * mm, "end": v(-5305.88, -21826.25) * mm});
            skLineSegment(sketch, "E350", {"start": v(-5305.88, -21826.25) * mm, "end": v(-5307.79, -21558.4) * mm});
            skLineSegment(sketch, "E351", {"start": v(-5307.79, -21558.4) * mm, "end": v(-5308.9, -21290.58) * mm});
            skLineSegment(sketch, "E352", {"start": v(-5308.9, -21290.58) * mm, "end": v(-5294.3, -20804.07) * mm});
            skLineSegment(sketch, "E353", {"start": v(-5294.3, -20804.07) * mm, "end": v(-5291.58, -20739.35) * mm});
            skLineSegment(sketch, "E354", {"start": v(-5291.58, -20739.35) * mm, "end": v(-5164.68, -20744.71) * mm});
            skLineSegment(sketch, "E355", {"start": v(-5164.68, -20744.71) * mm, "end": v(-5291.58, -20739.35) * mm});
            skLineSegment(sketch, "E356", {"start": v(-5291.58, -20739.35) * mm, "end": v(-5282.13, -20552.61) * mm});
            skLineSegment(sketch, "E357", {"start": v(-5282.13, -20552.61) * mm, "end": v(-5267.3, -20366.28) * mm});
            skLineSegment(sketch, "E358", {"start": v(-5267.3, -20366.28) * mm, "end": v(-5245.56, -20179.8) * mm});
            skLineSegment(sketch, "E359", {"start": v(-5245.56, -20179.8) * mm, "end": v(-5224.8, -19993.2) * mm});
            skLineSegment(sketch, "E360", {"start": v(-5224.8, -19993.2) * mm, "end": v(-5213.9, -19849.39) * mm});
            skLineSegment(sketch, "E361", {"start": v(-5213.9, -19849.39) * mm, "end": v(-5201.08, -19705.88) * mm});
            skLineSegment(sketch, "E362", {"start": v(-5201.08, -19705.88) * mm, "end": v(-5165.73, -19490.56) * mm});
            skLineSegment(sketch, "E363", {"start": v(-5165.73, -19490.56) * mm, "end": v(-5118.94, -19276.77) * mm});
            skLineSegment(sketch, "E364", {"start": v(-5118.94, -19276.77) * mm, "end": v(-5081.5, -19114.21) * mm});
            skLineSegment(sketch, "E365", {"start": v(-5081.5, -19114.21) * mm, "end": v(-5038.17, -18953.56) * mm});
            skLineSegment(sketch, "E366", {"start": v(-5038.17, -18953.56) * mm, "end": v(-4983.45, -18792.52) * mm});
            skLineSegment(sketch, "E367", {"start": v(-4983.45, -18792.52) * mm, "end": v(-4924.43, -18632.6) * mm});
            skLineSegment(sketch, "E368", {"start": v(-4924.43, -18632.6) * mm, "end": v(-4843.12, -18404.76) * mm});
            skLineSegment(sketch, "E369", {"start": v(-4843.12, -18404.76) * mm, "end": v(-4750.61, -18182.03) * mm});
            skLineSegment(sketch, "E370", {"start": v(-4750.61, -18182.03) * mm, "end": v(-4677.64, -18044.46) * mm});
            skLineSegment(sketch, "E371", {"start": v(-4677.64, -18044.46) * mm, "end": v(-4565.45, -18104) * mm});
            skLineSegment(sketch, "E372", {"start": v(-4565.45, -18104) * mm, "end": v(-4677.64, -18044.46) * mm});
            skLineSegment(sketch, "E373", {"start": v(-4677.64, -18044.46) * mm, "end": v(-4550.92, -17843.02) * mm});
            skLineSegment(sketch, "E374", {"start": v(-4550.92, -17843.02) * mm, "end": v(-4368.93, -17580.69) * mm});
            skLineSegment(sketch, "E375", {"start": v(-4368.93, -17580.69) * mm, "end": v(-4161.05, -17299.53) * mm});
            skLineSegment(sketch, "E376", {"start": v(-4161.05, -17299.53) * mm, "end": v(-4029.89, -17145.3) * mm});
            skLineSegment(sketch, "E377", {"start": v(-4029.89, -17145.3) * mm, "end": v(-3889.83, -16999.08) * mm});
            skLineSegment(sketch, "E378", {"start": v(-3889.83, -16999.08) * mm, "end": v(-3714.42, -16835.45) * mm});
            skLineSegment(sketch, "E379", {"start": v(-3714.42, -16835.45) * mm, "end": v(-3532.7, -16678.6) * mm});
            skLineSegment(sketch, "E380", {"start": v(-3532.7, -16678.6) * mm, "end": v(-3372.56, -16546.1) * mm});
            skLineSegment(sketch, "E381", {"start": v(-3372.56, -16546.1) * mm, "end": v(-3207.3, -16420.41) * mm});
            skLineSegment(sketch, "E382", {"start": v(-3207.3, -16420.41) * mm, "end": v(-3008.66, -16289.78) * mm});
            skLineSegment(sketch, "E383", {"start": v(-3008.66, -16289.78) * mm, "end": v(-2802.23, -16171.5) * mm});
            skLineSegment(sketch, "E384", {"start": v(-2802.23, -16171.5) * mm, "end": v(-2709.32, -16122.4) * mm});
            skLineSegment(sketch, "E385", {"start": v(-2709.32, -16122.4) * mm, "end": v(-2649.98, -16234.69) * mm});
            skLineSegment(sketch, "E386", {"start": v(-2649.98, -16234.69) * mm, "end": v(-2709.32, -16122.4) * mm});
            skLineSegment(sketch, "E387", {"start": v(-2709.32, -16122.4) * mm, "end": v(-2582.21, -16059.38) * mm});
            skLineSegment(sketch, "E388", {"start": v(-2582.21, -16059.38) * mm, "end": v(-2452.9, -16001) * mm});
            skLineSegment(sketch, "E389", {"start": v(-2452.9, -16001) * mm, "end": v(-2168.3, -15890.57) * mm});
            skLineSegment(sketch, "E390", {"start": v(-2168.3, -15890.57) * mm, "end": v(-1892.83, -15798.47) * mm});
            skLineSegment(sketch, "E391", {"start": v(-1892.83, -15798.47) * mm, "end": v(-1748.33, -15759.1) * mm});
            skLineSegment(sketch, "E392", {"start": v(-1748.33, -15759.1) * mm, "end": v(-1601.85, -15728.5) * mm});
            skLineSegment(sketch, "E393", {"start": v(-1601.85, -15728.5) * mm, "end": v(-1474.09, -15709.8) * mm});
            skLineSegment(sketch, "E394", {"start": v(-1474.09, -15709.8) * mm, "end": v(-1346, -15693.14) * mm});
            skLineSegment(sketch, "E395", {"start": v(-1346, -15693.14) * mm, "end": v(-1193.42, -15669.9) * mm});
            skLineSegment(sketch, "E396", {"start": v(-1193.42, -15669.9) * mm, "end": v(-1040.71, -15647.9) * mm});
            skLineSegment(sketch, "E397", {"start": v(-1040.71, -15647.9) * mm, "end": v(-899.95, -15634.16) * mm});
            skLineSegment(sketch, "E398", {"start": v(-899.95, -15634.16) * mm, "end": v(-758.65, -15625.98) * mm});
            skLineSegment(sketch, "E399", {"start": v(-758.65, -15625.98) * mm, "end": v(-535.5, -15618.69) * mm});
            skLineSegment(sketch, "E400", {"start": v(-535.5, -15618.69) * mm, "end": v(-298.86, -15611.02) * mm});
            skLineSegment(sketch, "E401", {"start": v(-298.86, -15611.02) * mm, "end": v(0, -15610.54) * mm});
            skLineSegment(sketch, "E402", {"start": v(0, -15610.54) * mm, "end": v(0.2, -15737.54) * mm});
            skLineSegment(sketch, "E403", {"start": v(0.2, -15737.54) * mm, "end": v(0, -15610.54) * mm});
            skLineSegment(sketch, "E404", {"start": v(0, -15610.54) * mm, "end": v(298.86, -15611.02) * mm});
            skLineSegment(sketch, "E405", {"start": v(298.86, -15611.02) * mm, "end": v(535.53, -15618.69) * mm});
            skLineSegment(sketch, "E406", {"start": v(535.53, -15618.69) * mm, "end": v(758.65, -15625.98) * mm});
            skLineSegment(sketch, "E407", {"start": v(758.65, -15625.98) * mm, "end": v(899.95, -15634.16) * mm});
            skLineSegment(sketch, "E408", {"start": v(899.95, -15634.16) * mm, "end": v(1040.71, -15647.9) * mm});
            skLineSegment(sketch, "E409", {"start": v(1040.71, -15647.9) * mm, "end": v(1193.42, -15669.9) * mm});
            skLineSegment(sketch, "E410", {"start": v(1193.42, -15669.9) * mm, "end": v(1346, -15693.14) * mm});
            skLineSegment(sketch, "E411", {"start": v(1346, -15693.14) * mm, "end": v(1474.09, -15709.8) * mm});
            skLineSegment(sketch, "E412", {"start": v(1474.09, -15709.8) * mm, "end": v(1601.85, -15728.5) * mm});
            skLineSegment(sketch, "E413", {"start": v(1601.85, -15728.5) * mm, "end": v(1748.33, -15759.1) * mm});
            skLineSegment(sketch, "E414", {"start": v(1748.33, -15759.1) * mm, "end": v(1892.83, -15798.47) * mm});
            skLineSegment(sketch, "E415", {"start": v(1892.83, -15798.47) * mm, "end": v(2168.3, -15890.57) * mm});
            skLineSegment(sketch, "E416", {"start": v(2168.3, -15890.57) * mm, "end": v(2452.93, -16001) * mm});
            skLineSegment(sketch, "E417", {"start": v(2452.93, -16001) * mm, "end": v(2582.19, -16059.38) * mm});
            skLineSegment(sketch, "E418", {"start": v(2582.19, -16059.38) * mm, "end": v(2709.27, -16122.37) * mm});
            skLineSegment(sketch, "E419", {"start": v(2709.27, -16122.37) * mm, "end": v(2652.88, -16236.16) * mm});
            skLineSegment(sketch, "E420", {"start": v(2652.88, -16236.16) * mm, "end": v(2709.27, -16122.37) * mm});
            skLineSegment(sketch, "E421", {"start": v(2709.27, -16122.37) * mm, "end": v(2802.23, -16171.5) * mm});
            skLineSegment(sketch, "E422", {"start": v(2802.23, -16171.5) * mm, "end": v(3008.68, -16289.78) * mm});
            skLineSegment(sketch, "E423", {"start": v(3008.68, -16289.78) * mm, "end": v(3207.3, -16420.41) * mm});
            skLineSegment(sketch, "E424", {"start": v(3207.3, -16420.41) * mm, "end": v(3372.59, -16546.1) * mm});
            skLineSegment(sketch, "E425", {"start": v(3372.59, -16546.1) * mm, "end": v(3532.7, -16678.6) * mm});
            skLineSegment(sketch, "E426", {"start": v(3532.7, -16678.6) * mm, "end": v(3714.42, -16835.45) * mm});
            skLineSegment(sketch, "E427", {"start": v(3714.42, -16835.45) * mm, "end": v(3889.83, -16999.08) * mm});
            skLineSegment(sketch, "E428", {"start": v(3889.83, -16999.08) * mm, "end": v(4029.89, -17145.3) * mm});
            skLineSegment(sketch, "E429", {"start": v(4029.89, -17145.3) * mm, "end": v(4161.05, -17299.53) * mm});
            skLineSegment(sketch, "E430", {"start": v(4161.05, -17299.53) * mm, "end": v(4368.93, -17580.69) * mm});
            skLineSegment(sketch, "E431", {"start": v(4368.93, -17580.69) * mm, "end": v(4550.92, -17843.02) * mm});
            skLineSegment(sketch, "E432", {"start": v(4550.92, -17843.02) * mm, "end": v(4677.61, -18044.44) * mm});
            skLineSegment(sketch, "E433", {"start": v(4677.61, -18044.44) * mm, "end": v(4570.12, -18112.05) * mm});
            skLineSegment(sketch, "E434", {"start": v(4570.12, -18112.05) * mm, "end": v(4677.61, -18044.44) * mm});
            skLineSegment(sketch, "E435", {"start": v(4677.61, -18044.44) * mm, "end": v(4750.64, -18182.03) * mm});
            skLineSegment(sketch, "E436", {"start": v(4750.64, -18182.03) * mm, "end": v(4843.12, -18404.76) * mm});
            skLineSegment(sketch, "E437", {"start": v(4843.12, -18404.76) * mm, "end": v(4924.43, -18632.6) * mm});
            skLineSegment(sketch, "E438", {"start": v(4924.43, -18632.6) * mm, "end": v(4983.45, -18792.52) * mm});
            skLineSegment(sketch, "E439", {"start": v(4983.45, -18792.52) * mm, "end": v(5038.2, -18953.56) * mm});
            skLineSegment(sketch, "E440", {"start": v(5038.2, -18953.56) * mm, "end": v(5081.5, -19114.21) * mm});
            skLineSegment(sketch, "E441", {"start": v(5081.5, -19114.21) * mm, "end": v(5118.94, -19276.77) * mm});
            skLineSegment(sketch, "E442", {"start": v(5118.94, -19276.77) * mm, "end": v(5165.73, -19490.56) * mm});
            skLineSegment(sketch, "E443", {"start": v(5165.73, -19490.56) * mm, "end": v(5201.08, -19705.88) * mm});
            skLineSegment(sketch, "E444", {"start": v(5201.08, -19705.88) * mm, "end": v(5213.9, -19849.39) * mm});
            skLineSegment(sketch, "E445", {"start": v(5213.9, -19849.39) * mm, "end": v(5224.8, -19993.2) * mm});
            skLineSegment(sketch, "E446", {"start": v(5224.8, -19993.2) * mm, "end": v(5245.56, -20179.8) * mm});
            skLineSegment(sketch, "E447", {"start": v(5245.56, -20179.8) * mm, "end": v(5267.3, -20366.28) * mm});
            skLineSegment(sketch, "E448", {"start": v(5267.3, -20366.28) * mm, "end": v(5282.13, -20552.56) * mm});
            skLineSegment(sketch, "E449", {"start": v(5282.13, -20552.56) * mm, "end": v(5291.58, -20739.3) * mm});
            skLineSegment(sketch, "E450", {"start": v(5291.58, -20739.3) * mm, "end": v(5164.76, -20745.73) * mm});
            skLineSegment(sketch, "E451", {"start": v(5164.76, -20745.73) * mm, "end": v(5291.58, -20739.3) * mm});
            skLineSegment(sketch, "E452", {"start": v(5291.58, -20739.3) * mm, "end": v(5294.33, -20804.07) * mm});
            skLineSegment(sketch, "E453", {"start": v(5294.33, -20804.07) * mm, "end": v(5308.9, -21290.58) * mm});
            skLineSegment(sketch, "E454", {"start": v(5308.9, -21290.58) * mm, "end": v(5307.79, -21558.4) * mm});
            skLineSegment(sketch, "E455", {"start": v(5307.79, -21558.4) * mm, "end": v(5305.88, -21826.25) * mm});
            skLineSegment(sketch, "E456", {"start": v(5305.88, -21826.25) * mm, "end": v(5311.9, -22275.7) * mm});
            skLineSegment(sketch, "E457", {"start": v(5311.9, -22275.7) * mm, "end": v(5310.63, -22650.96) * mm});
            skLineSegment(sketch, "E458", {"start": v(5310.63, -22650.96) * mm, "end": v(5297.98, -23025.99) * mm});
            skLineSegment(sketch, "E459", {"start": v(5297.98, -23025.99) * mm, "end": v(5282.74, -23275.75) * mm});
            skLineSegment(sketch, "E460", {"start": v(5282.74, -23275.75) * mm, "end": v(5262.17, -23525.07) * mm});
            skLineSegment(sketch, "E461", {"start": v(5262.17, -23525.07) * mm, "end": v(5135.6, -23514.63) * mm});
            skLineSegment(sketch, "E462", {"start": v(5135.6, -23514.63) * mm, "end": v(5262.17, -23525.07) * mm});
            skLineSegment(sketch, "E463", {"start": v(5262.17, -23525.07) * mm, "end": v(5235.27, -23854.9) * mm});
            skLineSegment(sketch, "E464", {"start": v(5235.27, -23854.9) * mm, "end": v(5209.26, -24211.84) * mm});
            skLineSegment(sketch, "E465", {"start": v(5209.26, -24211.84) * mm, "end": v(5179.85, -24568.45) * mm});
            skLineSegment(sketch, "E466", {"start": v(5179.85, -24568.45) * mm, "end": v(5140.6, -24925) * mm});
            skLineSegment(sketch, "E467", {"start": v(5140.6, -24925) * mm, "end": v(5097.98, -25281.26) * mm});
            skLineSegment(sketch, "E468", {"start": v(5097.98, -25281.26) * mm, "end": v(5061.48, -25607.31) * mm});
            skLineSegment(sketch, "E469", {"start": v(5061.48, -25607.31) * mm, "end": v(5021.17, -25932.84) * mm});
            skLineSegment(sketch, "E470", {"start": v(5021.17, -25932.84) * mm, "end": v(4963.97, -26295.68) * mm});
            skLineSegment(sketch, "E471", {"start": v(4963.97, -26295.68) * mm, "end": v(4838.52, -26275.92) * mm});
            skLineSegment(sketch, "E472", {"start": v(4838.52, -26275.92) * mm, "end": v(4963.97, -26295.68) * mm});
            skLineSegment(sketch, "E473", {"start": v(4963.97, -26295.68) * mm, "end": v(4881.52, -26758.19) * mm});
            skLineSegment(sketch, "E474", {"start": v(4881.52, -26758.19) * mm, "end": v(4780.97, -27334.26) * mm});
            skLineSegment(sketch, "E475", {"start": v(4780.97, -27334.26) * mm, "end": v(4666.13, -27907.26) * mm});
            skLineSegment(sketch, "E476", {"start": v(4666.13, -27907.26) * mm, "end": v(4565.1, -28314.27) * mm});
            skLineSegment(sketch, "E477", {"start": v(4565.1, -28314.27) * mm, "end": v(4456.38, -28719.53) * mm});
            skLineSegment(sketch, "E478", {"start": v(4456.38, -28719.53) * mm, "end": v(4376.32, -29019.22) * mm});
            skLineSegment(sketch, "E479", {"start": v(4376.32, -29019.22) * mm, "end": v(4298.52, -29061.56) * mm});
            skLineSegment(sketch, "E480", {"start": v(4298.52, -29061.56) * mm, "end": v(4208.73, -29108.25) * mm});
            skLineSegment(sketch, "E481", {"start": v(4208.73, -29108.25) * mm, "end": v(4121.66, -29149.78) * mm});
            skLineSegment(sketch, "E482", {"start": v(4121.66, -29149.78) * mm, "end": v(4026.61, -29205.78) * mm});
            skLineSegment(sketch, "E483", {"start": v(4026.61, -29205.78) * mm, "end": v(3905.7, -29285.16) * mm});
            skLineSegment(sketch, "E484", {"start": v(3905.7, -29285.16) * mm, "end": v(3850.1, -29332.76) * mm});
            skLineSegment(sketch, "E485", {"start": v(3850.1, -29332.76) * mm, "end": v(3798.27, -29384.83) * mm});
            skLineSegment(sketch, "E486", {"start": v(3798.27, -29384.83) * mm, "end": v(3729.74, -29461.66) * mm});
            skLineSegment(sketch, "E487", {"start": v(3729.74, -29461.66) * mm, "end": v(3666.5, -29542.56) * mm});
            skLineSegment(sketch, "E488", {"start": v(3666.5, -29542.56) * mm, "end": v(3593.97, -29651.27) * mm});
            skLineSegment(sketch, "E489", {"start": v(3593.97, -29651.27) * mm, "end": v(3525.52, -29762.93) * mm});
            skLineSegment(sketch, "E490", {"start": v(3525.52, -29762.93) * mm, "end": v(3434.44, -29914.44) * mm});
            skLineSegment(sketch, "E491", {"start": v(3434.44, -29914.44) * mm, "end": v(3362.4, -30059.33) * mm});
            skLineSegment(sketch, "E492", {"start": v(3362.4, -30059.33) * mm, "end": v(3300.9, -30209.29) * mm});
            skLineSegment(sketch, "E493", {"start": v(3300.9, -30209.29) * mm, "end": v(3215.3, -30455.87) * mm});
            skLineSegment(sketch, "E494", {"start": v(3215.3, -30455.87) * mm, "end": v(3129.86, -30739.92) * mm});
            skLineSegment(sketch, "E495", {"start": v(3129.86, -30739.92) * mm, "end": v(3068.22, -30964) * mm});
            skLineSegment(sketch, "E496", {"start": v(3068.22, -30964) * mm, "end": v(3030.32, -31159.25) * mm});
            skLineSegment(sketch, "E497", {"start": v(3030.32, -31159.25) * mm, "end": v(3006.83, -31357.01) * mm});
            skLineSegment(sketch, "E498", {"start": v(3006.83, -31357.01) * mm, "end": v(2997.84, -31496.94) * mm});
            skLineSegment(sketch, "E499", {"start": v(2997.84, -31496.94) * mm, "end": v(2996.8, -31637.07) * mm});
            skLineSegment(sketch, "E500", {"start": v(2996.8, -31637.07) * mm, "end": v(3003.98, -31757.6) * mm});
            skLineSegment(sketch, "E501", {"start": v(3003.98, -31757.6) * mm, "end": v(3019.86, -31877.25) * mm});
            skLineSegment(sketch, "E502", {"start": v(3019.86, -31877.25) * mm, "end": v(3039.54, -31972.28) * mm});
            skLineSegment(sketch, "E503", {"start": v(3039.54, -31972.28) * mm, "end": v(3065.14, -32065.85) * mm});
            skLineSegment(sketch, "E504", {"start": v(3065.14, -32065.85) * mm, "end": v(3062.3, -32337.07) * mm});
            skLineSegment(sketch, "E505", {"start": v(3062.3, -32337.07) * mm, "end": v(3054.1, -32524.01) * mm});
            skLineSegment(sketch, "E506", {"start": v(3054.1, -32524.01) * mm, "end": v(3044.75, -32637.76) * mm});
            skLineSegment(sketch, "E507", {"start": v(3044.75, -32637.76) * mm, "end": v(2918.18, -32627.34) * mm});
            skLineSegment(sketch, "E508", {"start": v(2918.18, -32627.34) * mm, "end": v(3044.75, -32637.76) * mm});
            skLineSegment(sketch, "E509", {"start": v(3044.75, -32637.76) * mm, "end": v(2983.03, -32759.17) * mm});
            skLineSegment(sketch, "E510", {"start": v(2983.03, -32759.17) * mm, "end": v(2944.93, -32850.4) * mm});
            skLineSegment(sketch, "E511", {"start": v(2944.93, -32850.4) * mm, "end": v(2906.95, -32941.7) * mm});
            skLineSegment(sketch, "E512", {"start": v(2906.95, -32941.7) * mm, "end": v(2867.56, -33023.2) * mm});
            skLineSegment(sketch, "E513", {"start": v(2867.56, -33023.2) * mm, "end": v(2827.07, -33104.3) * mm});
            skLineSegment(sketch, "E514", {"start": v(2827.07, -33104.3) * mm, "end": v(2773.7, -33221.83) * mm});
            skLineSegment(sketch, "E515", {"start": v(2773.7, -33221.83) * mm, "end": v(2718.61, -33338.34) * mm});
            skLineSegment(sketch, "E516", {"start": v(2718.61, -33338.34) * mm, "end": v(2673.78, -33419.11) * mm});
            skLineSegment(sketch, "E517", {"start": v(2673.78, -33419.11) * mm, "end": v(2627.8, -33499.32) * mm});
            skLineSegment(sketch, "E518", {"start": v(2627.8, -33499.32) * mm, "end": v(2559.99, -33629.14) * mm});
            skLineSegment(sketch, "E519", {"start": v(2559.99, -33629.14) * mm, "end": v(2492.45, -33759.06) * mm});
            skLineSegment(sketch, "E520", {"start": v(2492.45, -33759.06) * mm, "end": v(2394.2, -33928) * mm});
            skLineSegment(sketch, "E521", {"start": v(2394.2, -33928) * mm, "end": v(2322.78, -34052.36) * mm});
            skLineSegment(sketch, "E522", {"start": v(2322.78, -34052.36) * mm, "end": v(2249.3, -34175.37) * mm});
            skLineSegment(sketch, "E523", {"start": v(2249.3, -34175.37) * mm, "end": v(2132.91, -34350.45) * mm});
            skLineSegment(sketch, "E524", {"start": v(2132.91, -34350.45) * mm, "end": v(1987.45, -34573.95) * mm});
            skLineSegment(sketch, "E525", {"start": v(1987.45, -34573.95) * mm, "end": v(1861.18, -34755.18) * mm});
            skLineSegment(sketch, "E526", {"start": v(1861.18, -34755.18) * mm, "end": v(1682.83, -34989.97) * mm});
            skLineSegment(sketch, "E527", {"start": v(1682.83, -34989.97) * mm, "end": v(1516.74, -35190.89) * mm});
            skLineSegment(sketch, "E528", {"start": v(1516.74, -35190.89) * mm, "end": v(1310.92, -35415.17) * mm});
            skLineSegment(sketch, "E529", {"start": v(1310.92, -35415.17) * mm, "end": v(1165.1, -35560.33) * mm});
            skLineSegment(sketch, "E530", {"start": v(1165.1, -35560.33) * mm, "end": v(1059.9, -35649.92) * mm});
            skLineSegment(sketch, "E531", {"start": v(1059.9, -35649.92) * mm, "end": v(950.72, -35735.26) * mm});
            skLineSegment(sketch, "E532", {"start": v(950.72, -35735.26) * mm, "end": v(786.64, -35857.94) * mm});
            skLineSegment(sketch, "E533", {"start": v(786.64, -35857.94) * mm, "end": v(613.97, -35966.58) * mm});
            skLineSegment(sketch, "E534", {"start": v(613.97, -35966.58) * mm, "end": v(468.86, -36034.04) * mm});
            skLineSegment(sketch, "E535", {"start": v(468.86, -36034.04) * mm, "end": v(316.97, -36085.9) * mm});
            skLineSegment(sketch, "E536", {"start": v(316.97, -36085.9) * mm, "end": v(159.77, -36123.75) * mm});
            skLineSegment(sketch, "E537", {"start": v(159.77, -36123.75) * mm, "end": v(0, -36146.69) * mm});
            skSolve(sketch);
        }
        {
            var Q0;
            Q0 = qSketchRegion(id + "F0", true);
            extrude(context, id + "F1", {"entities" : qUnion([Q0]), "depth" : 4 * mm, "offsetDistance" : 25 * mm});
        }
    });
